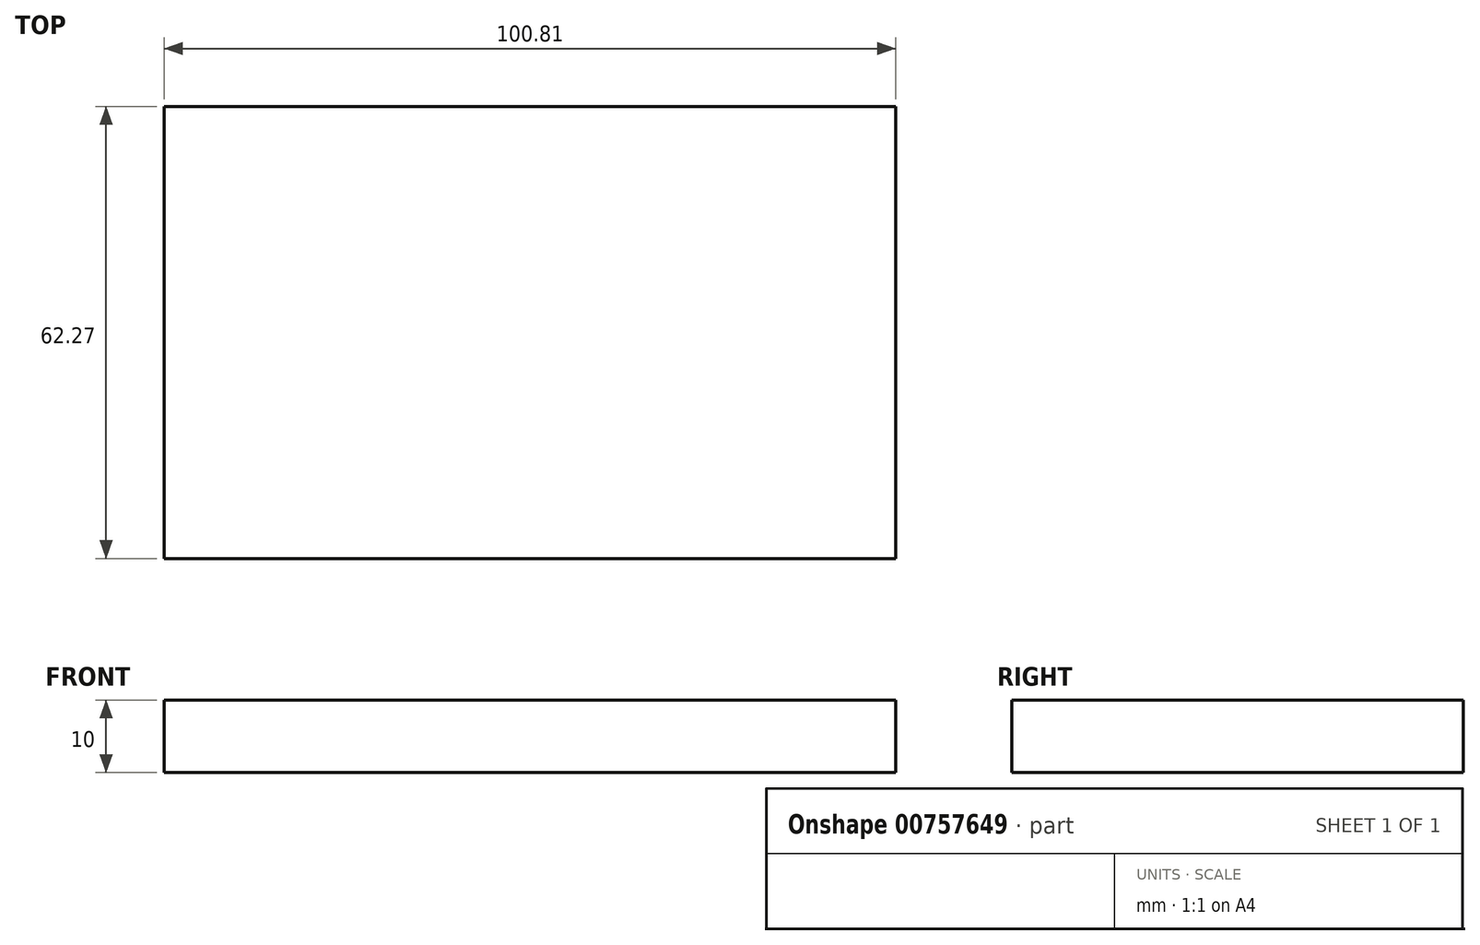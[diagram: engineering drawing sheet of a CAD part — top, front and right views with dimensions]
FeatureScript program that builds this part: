
annotation { "Feature Type Name" : "Feature", "Feature Type Description" : "" }
export const myFeature = defineFeature(function(context is Context, id is Id, definition is map)
    precondition{}
    {
        {
            var Q0;
            Q0=qCreatedBy(makeId("Top.planeOp"),FACE);
            var sketch = newSketch(context, id + "F0", { "sketchPlane" : qUnion([Q0])});
            skLineSegment(sketch, "E0.bottom", {"start": v(-56.76, 0) * mm, "end": v(44.05, 0) * mm});
            skLineSegment(sketch, "E0.top", {"start": v(-56.76, -62.27) * mm, "end": v(44.05, -62.27) * mm});
            skLineSegment(sketch, "E0.left", {"start": v(-56.76, 0) * mm, "end": v(-56.76, -62.27) * mm});
            skLineSegment(sketch, "E0.right", {"start": v(44.05, 0) * mm, "end": v(44.05, -62.27) * mm});
            skLineSegment(sketch, "E1.bottom", {"start": v(44.05, 32.45) * mm, "end": v(-65.3, 32.45) * mm});
            skLineSegment(sketch, "E1.top", {"start": v(44.05, 67.92) * mm, "end": v(-65.3, 67.92) * mm});
            skLineSegment(sketch, "E1.left", {"start": v(44.05, 32.45) * mm, "end": v(44.05, 67.92) * mm});
            skLineSegment(sketch, "E1.right", {"start": v(-65.3, 32.45) * mm, "end": v(-65.3, 67.92) * mm});
            skSolve(sketch);
        }
        {
            var Q0;
            Q0=makeQuery(id+"F0.imprint","IMPRINT",FACE,{"disambiguationData":[TD([[makeQuery(id+"F0.imprint","IMPRINT",EDGE,{"derivedFrom":sQuery(id+"F0.wireOp",EDGE,"E0.bottom")}),-1.0]])]});
            extrude(context, id + "F1", {"entities" : qUnion([Q0]), "depth" : 10 * mm, "offsetDistance" : 25 * mm});
        }
    });
